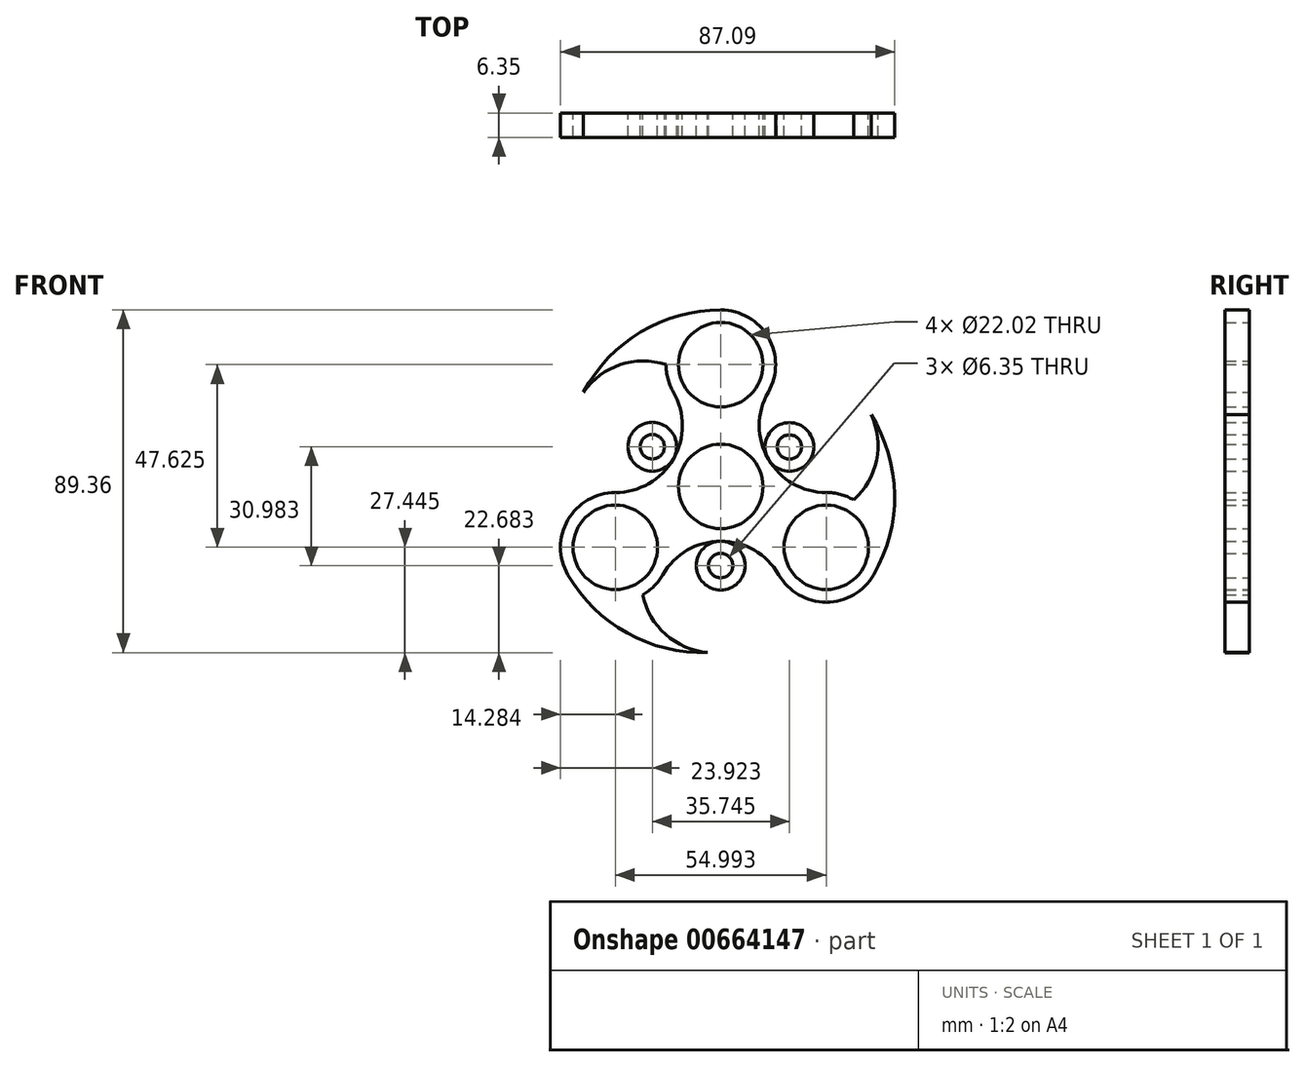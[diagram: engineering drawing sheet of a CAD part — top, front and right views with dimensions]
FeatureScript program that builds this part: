
annotation { "Feature Type Name" : "Feature", "Feature Type Description" : "" }
export const myFeature = defineFeature(function(context is Context, id is Id, definition is map)
    precondition{}
    {
        {
            var Q0;
            Q0=qCreatedBy(makeId("Front.planeOp"),FACE);
            var sketch = newSketch(context, id + "F0", { "sketchPlane" : qUnion([Q0])});
            skCircle(sketch, "E0", {"center": v(0, 31.75) * mm, "radius": 14.29 * mm});
            skCircle(sketch, "E1", {"center": v(0, 31.75) * mm, "radius": 11.01 * mm});
            skCircle(sketch, "E2", {"center": v(0, 0) * mm, "radius": 14.29 * mm});
            skCircle(sketch, "E3", {"center": v(0, 0) * mm, "radius": 11.01 * mm});
            skCircle(sketch, "E4.1.0", {"center": v(-27.5, -15.87) * mm, "radius": 11.01 * mm});
            skCircle(sketch, "E4.1.1", {"center": v(-27.5, -15.87) * mm, "radius": 14.29 * mm});
            skCircle(sketch, "E4.2.0", {"center": v(27.5, -15.88) * mm, "radius": 11.01 * mm});
            skCircle(sketch, "E4.2.1", {"center": v(27.5, -15.88) * mm, "radius": 14.29 * mm});
            skArc(sketch, "E5", {"start": v(-27.5, -1.59) * mm, "mid": v(-12.37, 7.14) * mm, "end": v(-12.37, 24.6) * mm});
            skArc(sketch, "E6.1.0", {"start": v(15.12, -23.02) * mm, "mid": v(0, -14.29) * mm, "end": v(-15.12, -23.02) * mm});
            skArc(sketch, "E6.2.0", {"start": v(12.37, 24.6) * mm, "mid": v(12.37, 7.14) * mm, "end": v(27.5, -1.59) * mm});
            skArc(sketch, "E7", {"start": v(0, 46.04) * mm, "mid": v(-20.86, 40.27) * mm, "end": v(-35.79, 24.6) * mm});
            skArc(sketch, "E8", {"start": v(-14.29, 31.75) * mm, "mid": v(-26.23, 31.76) * mm, "end": v(-35.79, 24.6) * mm});
            skArc(sketch, "E9.1.0", {"start": v(-20.35, -28.25) * mm, "mid": v(-14.39, -38.6) * mm, "end": v(-3.42, -43.3) * mm});
            skArc(sketch, "E9.1.1", {"start": v(-39.87, -23.02) * mm, "mid": v(-24.45, -38.2) * mm, "end": v(-3.42, -43.3) * mm});
            skArc(sketch, "E9.2.0", {"start": v(34.64, -3.5) * mm, "mid": v(40.62, 6.83) * mm, "end": v(39.2, 18.69) * mm});
            skArc(sketch, "E9.2.1", {"start": v(39.87, -23.02) * mm, "mid": v(45.3, -2.07) * mm, "end": v(39.2, 18.69) * mm});
            skCircle(sketch, "E10", {"center": v(-17.86, 10.35) * mm, "radius": 6.35 * mm});
            skCircle(sketch, "E11", {"center": v(-17.86, 10.35) * mm, "radius": 3.18 * mm});
            skCircle(sketch, "E12.1.0", {"center": v(-0.03, -20.64) * mm, "radius": 6.35 * mm});
            skCircle(sketch, "E12.1.1", {"center": v(-0.03, -20.64) * mm, "radius": 3.18 * mm});
            skCircle(sketch, "E12.2.0", {"center": v(17.89, 10.3) * mm, "radius": 6.35 * mm});
            skCircle(sketch, "E12.2.1", {"center": v(17.89, 10.3) * mm, "radius": 3.18 * mm});
            skSolve(sketch);
        }
        {
            var Q0;
            Q0=qSketchRegion(id+"F0",true);
            extrude(context, id + "F1", {"entities" : qUnion([Q0]), "depth" : 6.35 * mm, "offsetDistance" : 25.4 * mm});
        }
    });
